# Revit family: Burko F-2910 Triplex
name_source: partatom
category: HLS-Bauteile
units: mm (PartAtom-declared; Revit-internal decimal feet)

## family parameters
Arbeitsebenenbasiert = Nein
Beim Laden mit Abzugskörper schneiden = Nein
Bemaßung runder Anschluss = Durchmesser verwenden
Beschriftungsausrichtung beibehalten = Nein
Gemeinsam genutzt = Nein
Immer vertikal = Ja
Klassifizierung = Keine
Raumberechnungspunkt = Nein
Teiletyp = Normal

## types (5) — shared parameters
Anschluss 1" = 25 mm  [stored 0.082021 ft]
Anschluss 2" = 50 mm  [stored 0.164042 ft]
Datenblatt = https://www.burkhalter-h2o.ch
Homepage = https://www.burkhalter-h2o.ch
LUT = LUT_Burko_F-2910 Triplex
Sockel_Höhe = 200 mm  [stored 0.656168 ft]
Steuerung_Breite = 220 mm  [stored 0.721785 ft]
Steuerung_Höhe = 300 mm  [stored 0.984252 ft]
Steuerung_Tiefe = 75 mm  [stored 0.246063 ft]
zero-valued in all types: Vorgabe-Ansicht

## per-type parameters (varying)
| type | A | B | Behälterkopf | C | F | Harzinhalt_pro_Harzdruckbehälter | Sockel_Absatz_Oben | Sockel_Absatz_Unten |
| Burko F-2910 - 150L | 552 mm  [stored 1.81102 ft] | 1960 mm  [stored 6.43045 ft] | 150 mm  [stored 0.492126 ft] | 1700 mm  [stored 5.57743 ft] | 925 mm  [stored 3.03478 ft] | 150L | 286 mm  [stored 0.93832 ft] | 286 mm  [stored 0.93832 ft] |
| Burko F-2910 - 200L | 552 mm  [stored 1.81102 ft] | 1960 mm  [stored 6.43045 ft] | 150 mm  [stored 0.492126 ft] | 1700 mm  [stored 5.57743 ft] | 925 mm  [stored 3.03478 ft] | 200L | 286 mm  [stored 0.93832 ft] | 286 mm  [stored 0.93832 ft] |
| Burko F-2910 - 250L | 610 mm  [stored 2.00131 ft] | 2180 mm  [stored 7.15223 ft] | 200 mm  [stored 0.656168 ft] | 1920 mm  [stored 6.29921 ft] | 925 mm  [stored 3.03478 ft] | 250L | 315 mm  [stored 1.03346 ft] | 315 mm  [stored 1.03346 ft] |
| Burko F-2910 - 300L | 610 mm  [stored 2.00131 ft] | 2180 mm  [stored 7.15223 ft] | 200 mm  [stored 0.656168 ft] | 1920 mm  [stored 6.29921 ft] | 1090 mm  [stored 3.57612 ft] | 300L | 315 mm  [stored 1.03346 ft] | 315 mm  [stored 1.03346 ft] |
| Burko F-2910 - 400L | 770 mm  [stored 2.52625 ft] | 2340 mm  [stored 7.67717 ft] | 250 mm  [stored 0.82021 ft] | 2080 mm  [stored 6.82415 ft] | 1090 mm  [stored 3.57612 ft] | 400L | 395 mm  [stored 1.29593 ft] | 395 mm  [stored 1.29593 ft] |

note: [stored X ft] marks values corroborated as IEEE doubles in the binary element streams (Revit-internal decimal feet)
